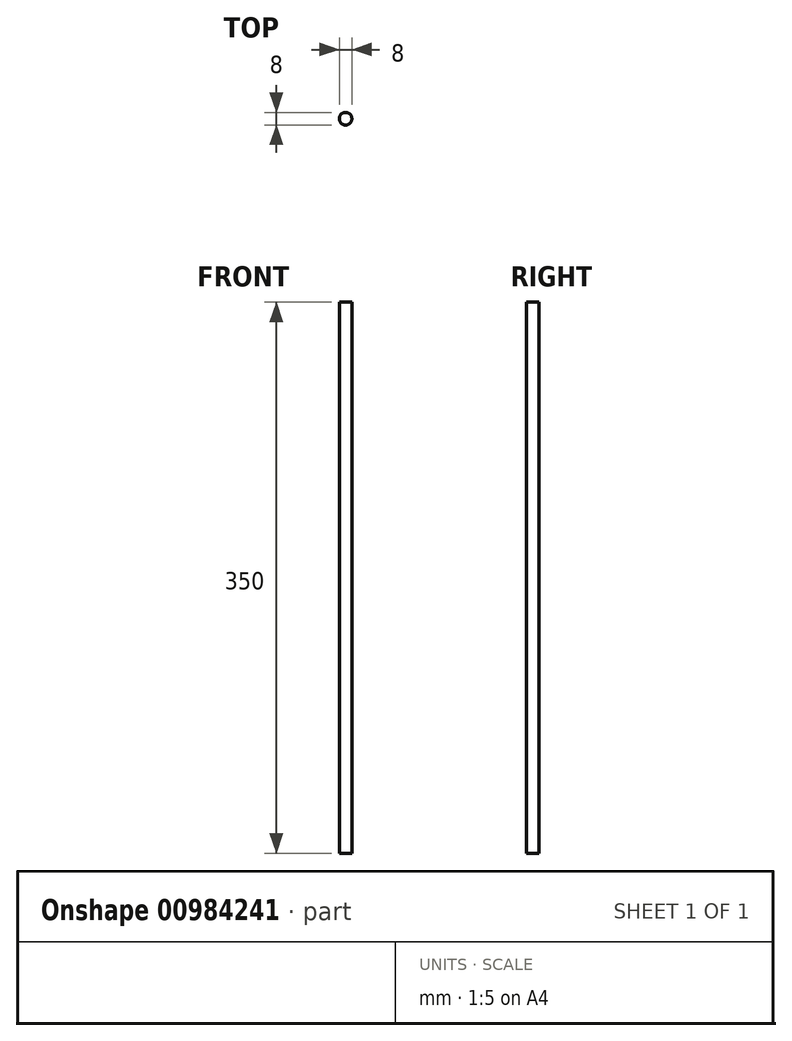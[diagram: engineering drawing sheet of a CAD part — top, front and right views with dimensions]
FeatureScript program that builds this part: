
annotation { "Feature Type Name" : "Feature", "Feature Type Description" : "" }
export const myFeature = defineFeature(function(context is Context, id is Id, definition is map)
    precondition{}
    {
        {
            var Q0;
            Q0=qCreatedBy(makeId("Top.planeOp"),FACE);
            var sketch = newSketch(context, id + "F0", { "sketchPlane" : qUnion([Q0])});
            skCircle(sketch, "E0", {"center": v(0, 0) * mm, "radius": 4 * mm});
            skSolve(sketch);
        }
        {
            var Q0;
            Q0=makeQuery(id+"F0.imprint","IMPRINT",FACE,{"disambiguationData":[TD([[makeQuery(id+"F0.imprint","IMPRINT",EDGE,{"derivedFrom":sQuery(id+"F0.wireOp",EDGE,"E0")}),1.0]])]});
            extrude(context, id + "F1", {"entities" : qUnion([Q0]), "oppositeDirection" : true, "depth" : 350 * mm, "offsetDistance" : 25 * mm});
        }
    });
